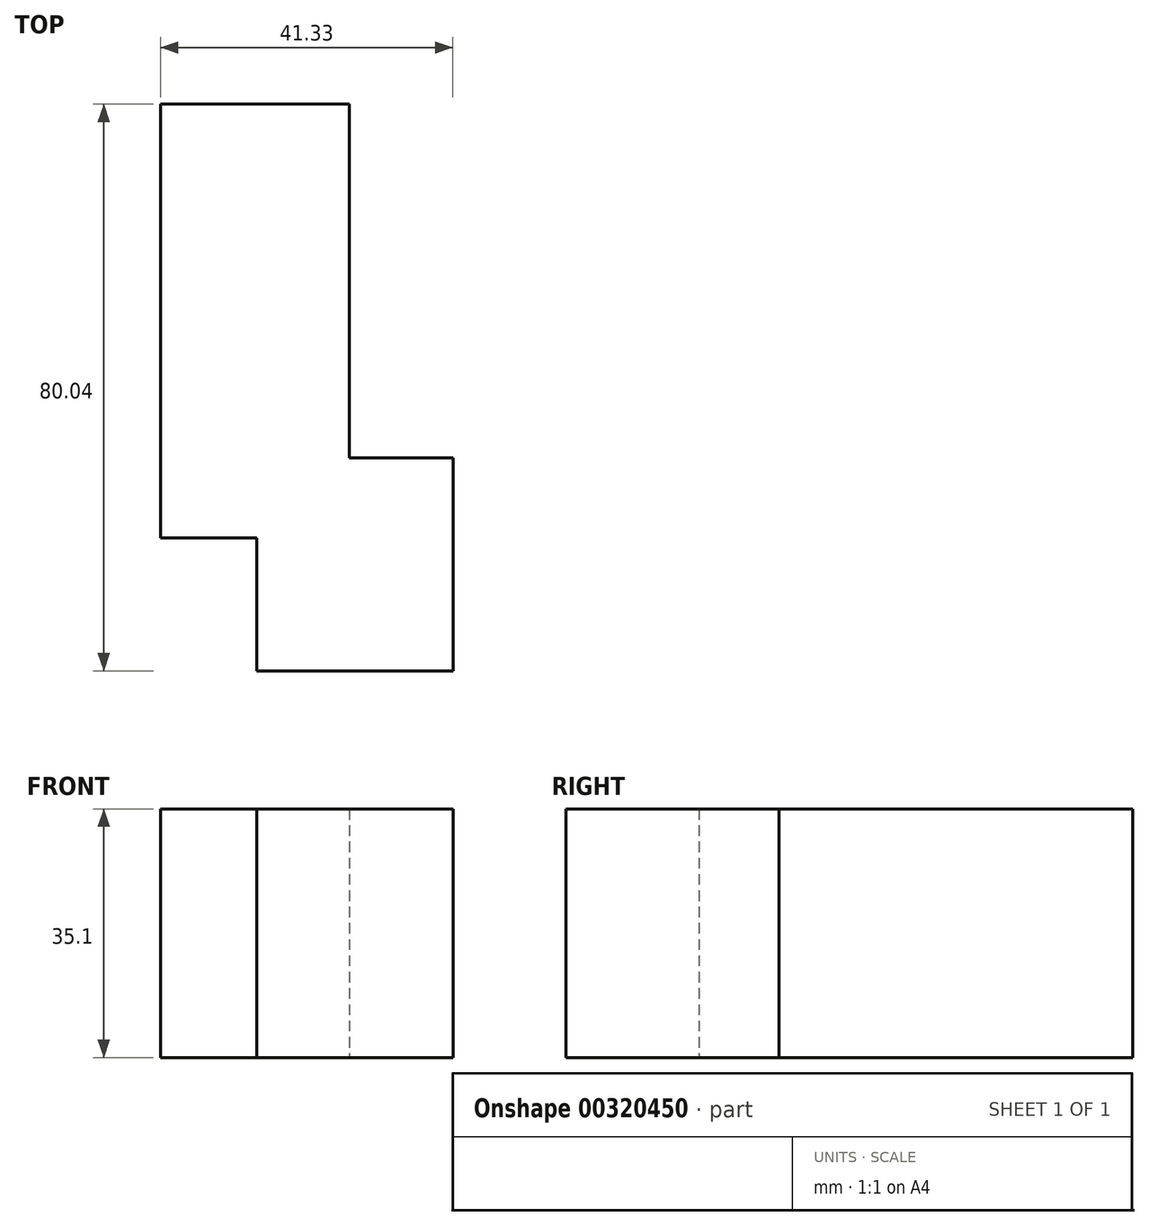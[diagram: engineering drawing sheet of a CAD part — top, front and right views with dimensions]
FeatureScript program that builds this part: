
annotation { "Feature Type Name" : "Feature", "Feature Type Description" : "" }
export const myFeature = defineFeature(function(context is Context, id is Id, definition is map)
    precondition{}
    {
        {
            var Q0;
            Q0=qCreatedBy(makeId("Top.planeOp"),FACE);
            var sketch = newSketch(context, id + "F0", { "sketchPlane" : qUnion([Q0])});
            skLineSegment(sketch, "E0.bottom", {"start": v(0, 0) * mm, "end": v(27.73, 0) * mm});
            skLineSegment(sketch, "E0.top", {"start": v(0, -30.06) * mm, "end": v(27.73, -30.06) * mm});
            skLineSegment(sketch, "E0.left", {"start": v(0, 0) * mm, "end": v(0, -30.06) * mm});
            skLineSegment(sketch, "E0.right", {"start": v(27.73, 0) * mm, "end": v(27.73, -30.06) * mm});
            skLineSegment(sketch, "E1.bottom", {"start": v(13.08, -11.28) * mm, "end": v(-13.6, -11.28) * mm});
            skLineSegment(sketch, "E1.top", {"start": v(13.08, 35.33) * mm, "end": v(-13.6, 35.33) * mm});
            skLineSegment(sketch, "E1.left", {"start": v(13.08, -11.28) * mm, "end": v(13.08, 35.33) * mm});
            skLineSegment(sketch, "E1.right", {"start": v(-13.6, -11.28) * mm, "end": v(-13.6, 35.33) * mm});
            skSolve(sketch);
        }
        {
            var Q0;
            {var subQ4=sQuery(id+"F0.wireOp",EDGE,"E1.top");Q0=makeQuery(id+"F0.imprint","IMPRINT",FACE,{"disambiguationData":[TD([[makeQuery(id+"F0.imprint","IMPRINT",EDGE,{"derivedFrom":subQ4}),1.0]])]});}
            var Q1;
            {var subQ2=sQuery(id+"F0.wireOp",EDGE,"E0.top");Q1=makeQuery(id+"F0.imprint","IMPRINT",FACE,{"disambiguationData":[TD([[makeQuery(id+"F0.imprint","IMPRINT",EDGE,{"derivedFrom":subQ2}),1.0]])]});}
            var Q2;
            {var subQ0=sQuery(id+"F0.wireOp",EDGE,"E0.left");var subQ1=sQuery(id+"F0.wireOp",EDGE,"E0.bottom");var subQ2=makeQuery(id+"F0.imprint","INTERSECT",VERTEX,{"derivedFrom":[subQ1,subQ0]});Q2=makeQuery(id+"F0.imprint","IMPRINT",FACE,{"disambiguationData":[TD([[makeQuery(id+"F0.imprint","IMPRINT",EDGE,{"disambiguationData":[TD([[subQ2,-1.0]])],"derivedFrom":subQ1}),-1.0]])]});}
            extrude(context, id + "F1", {"entities" : qUnion([Q0, Q1, Q2]), "depth" : 35.1 * mm});
        }
        {
            var Q0;
            Q0=makeQuery(id+"F1.opExtrude","SWEPT_FACE",FACE,{"disambiguationData":[OSD([sQuery(id+"F0.wireOp",EDGE,"E1.top")])]});
            extrude(context, id + "F2", {"entities" : qUnion([Q0]), "operationType" : NewBodyOperationType.ADD, "depth" : 14.65 * mm});
        }
    });
